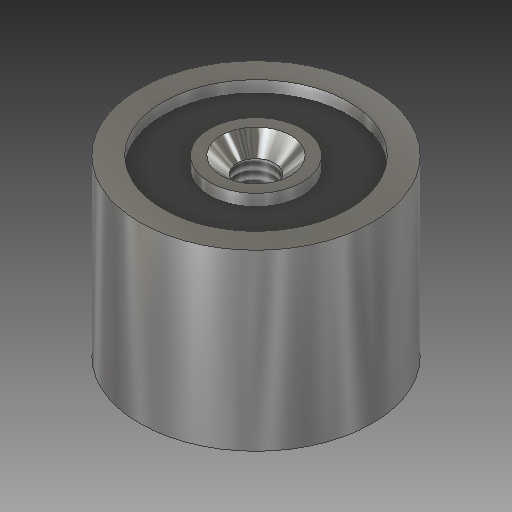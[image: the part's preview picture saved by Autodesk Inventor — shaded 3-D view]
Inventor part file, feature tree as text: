
AUTODESK INVENTOR PART (.ipt)
format: ipt  version: 2019 (Build 230136000, 136)  size: 185,344 bytes
history: native  units: mm
features: sketch x4, extrude x3, hole x1
ambient origin geometry x8: Origin, YZ Plane, XZ Plane, XY Plane, X Axis, Y Axis, Z Axis, Center Point
bodies: Solid1 (feature_tree)
feature tree (8):
  extrude  "Extrusion1"  Depth=15.0mm TaperAngle=0.0deg
  extrude  "Extrusion2"  Depth=8.0mm
  extrude  "Extrusion3"  Depth=8.0mm TaperAngle=0.0deg
  hole  "Hole2"  [1 undecoded]
  sketch  "Sketch1"  dims[d0=20.0mm d1=15.0mm d2=0.0mm]
  sketch  "Sketch2"  dims[d3=8.0mm d4=2.0mm]
  sketch  "Sketch3"  dims[d5=9.0mm d6=0.0mm d7=8.0mm d8=0.0mm]
  sketch  "Sketch5"  dims[d20=4.0mm d21=3.242mm d22=8.0mm d23=6.0mm d24=2.0mm d25=90.0deg d26=8.0mm d27=20.594885mm]
note: 1 required parameter value undecoded (feature->parameter linkage not recoverable at this tier; creation-order binding heuristic only, values carry confidence <= 0.55)
